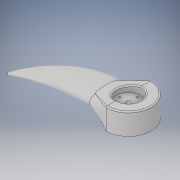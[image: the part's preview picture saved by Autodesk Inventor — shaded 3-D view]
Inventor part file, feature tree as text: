
AUTODESK INVENTOR PART (.ipt)
format: ipt  version: 2019 (Build 230136000, 136)  size: 368,128 bytes
history: native  units: mm
features: other x8, sketch x8, extrude x3, loft x2, fillet x2, revolve x1
ambient origin geometry x8: Origin, YZ Plane, XZ Plane, XY Plane, X Axis, Y Axis, Z Axis, Center Point
bodies: Body1 (feature_tree)
feature tree (24):
  other  "Твердое тело1"
  extrude  "Выдавливание1"  Depth=20.0mm TaperAngle=0.0deg
  other  "РабПлоскость5"
  loft  "Лофт3"
  other  "РабПлоскость6"
  sketch  "Эскиз11"
  revolve  "Вращение2"
  other  "РабПлоскость7"
  sketch  "Эскиз13"
  other  "РабПлоскость8"
  loft  "Лофт4"
  fillet  "Сопряжение3"  [1 undecoded]
  extrude  "Выдавливание5"  [1 undecoded]
  extrude  "Выдавливание6"  Depth=100.0mm
  fillet  "Сопряжение4"  Radius=3.333333mm
  sketch  "Эскиз1"
  sketch  "Эскиз10"
  other  "Ребра4"
  sketch  "Эскиз12"
  sketch  "Эскиз14"
  other  "Ребра5"
  other  "Ребра6"
  sketch  "Эскиз16"
  sketch  "Эскиз17"
note: 2 required parameter values undecoded (feature->parameter linkage not recoverable at this tier; creation-order binding heuristic only, values carry confidence <= 0.55)
